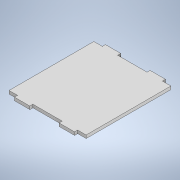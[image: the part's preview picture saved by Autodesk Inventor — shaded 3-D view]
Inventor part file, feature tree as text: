
AUTODESK INVENTOR PART (.ipt)
format: ipt  version: 2022 (Build 260153000, 153)  size: 126,976 bytes
history: native  units: mm
features: sheet_metal_op x1, sketch x1, other x1
ambient origin geometry x8: Origin, YZ Plane, XZ Plane, XY Plane, X Axis, Y Axis, Z Axis, Center Point
bodies: Solid1 (feature_tree)
feature tree (3):
  sheet_metal_op  "Face1"
  sketch  "Sketch1"  dims[d1=50.0mm d2=10.0mm d3=10.0mm d4=5.5mm d5=5.5mm d6=2.0mm d7=27.5mm d8=2.0mm]
  other  "Plate1"
